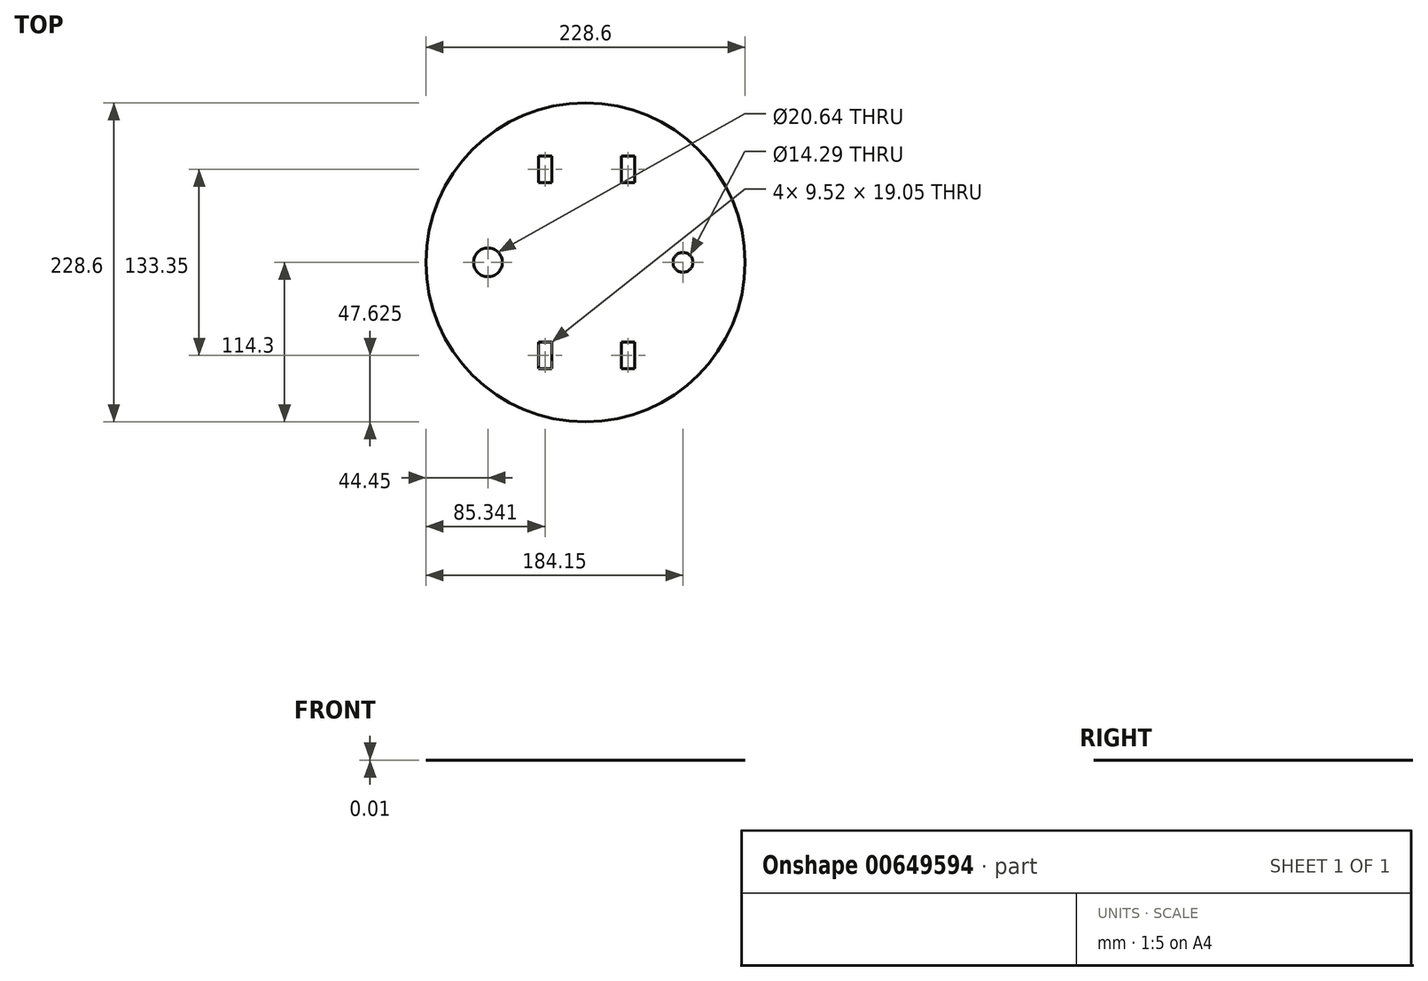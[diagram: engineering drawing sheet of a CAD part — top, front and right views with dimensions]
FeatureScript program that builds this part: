
annotation { "Feature Type Name" : "Feature", "Feature Type Description" : "" }
export const myFeature = defineFeature(function(context is Context, id is Id, definition is map)
    precondition{}
    {
        {
            var Q0;
            Q0=qCreatedBy(makeId("Top.planeOp"),FACE);
            var sketch = newSketch(context, id + "F0", { "sketchPlane" : qUnion([Q0])});
            skCircle(sketch, "E0", {"center": v(0, 0) * mm, "radius": 114.3 * mm});
            skLineSegment(sketch, "E1", {"start": v(-69.85, 0) * mm, "end": v(69.85, 0) * mm, "construction": true});
            skCircle(sketch, "E2", {"center": v(-69.85, 0) * mm, "radius": 10.32 * mm});
            skCircle(sketch, "E3", {"center": v(69.85, 0) * mm, "radius": 7.14 * mm});
            skLineSegment(sketch, "E4", {"start": v(29.75, 110.36) * mm, "end": v(29.75, -110.36) * mm, "construction": true});
            skLineSegment(sketch, "E5", {"start": v(-29.75, -110.36) * mm, "end": v(-29.75, 110.36) * mm, "construction": true});
            skLineSegment(sketch, "E6", {"start": v(29.75, 0) * mm, "end": v(-29.75, 0) * mm, "construction": true});
            skLineSegment(sketch, "E7.bottom", {"start": v(-24.2, 76.2) * mm, "end": v(-33.72, 76.2) * mm});
            skLineSegment(sketch, "E7.top", {"start": v(-24.2, 57.15) * mm, "end": v(-33.72, 57.15) * mm});
            skLineSegment(sketch, "E7.left", {"start": v(-24.2, 76.2) * mm, "end": v(-24.2, 57.15) * mm});
            skLineSegment(sketch, "E7.right", {"start": v(-33.72, 76.2) * mm, "end": v(-33.72, 57.15) * mm});
            skLineSegment(sketch, "E8.bottom", {"start": v(-24.2, -76.2) * mm, "end": v(-33.72, -76.2) * mm});
            skLineSegment(sketch, "E8.top", {"start": v(-24.2, -57.15) * mm, "end": v(-33.72, -57.15) * mm});
            skLineSegment(sketch, "E8.left", {"start": v(-24.2, -76.2) * mm, "end": v(-24.2, -57.15) * mm});
            skLineSegment(sketch, "E8.right", {"start": v(-33.72, -76.2) * mm, "end": v(-33.72, -57.15) * mm});
            skLineSegment(sketch, "E9.bottom", {"start": v(35.3, -76.2) * mm, "end": v(25.78, -76.2) * mm});
            skLineSegment(sketch, "E9.top", {"start": v(35.3, -57.15) * mm, "end": v(25.78, -57.15) * mm});
            skLineSegment(sketch, "E9.left", {"start": v(35.3, -76.2) * mm, "end": v(35.3, -57.15) * mm});
            skLineSegment(sketch, "E9.right", {"start": v(25.78, -76.2) * mm, "end": v(25.78, -57.15) * mm});
            skLineSegment(sketch, "E10.bottom", {"start": v(35.3, 57.15) * mm, "end": v(25.78, 57.15) * mm});
            skLineSegment(sketch, "E10.top", {"start": v(35.3, 76.2) * mm, "end": v(25.78, 76.2) * mm});
            skLineSegment(sketch, "E10.left", {"start": v(35.3, 57.15) * mm, "end": v(35.3, 76.2) * mm});
            skLineSegment(sketch, "E10.right", {"start": v(25.78, 57.15) * mm, "end": v(25.78, 76.2) * mm});
            skSolve(sketch);
        }
        {
            var Q0;
            Q0 = qSketchRegion(id + "F0", true);
            extrude(context, id + "F1", {"entities" : qUnion([Q0]), "depth" : 5 / 406.4 * mm, "offsetDistance" : 25.4 * mm});
        }
    });
